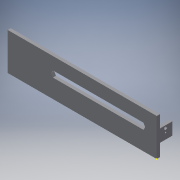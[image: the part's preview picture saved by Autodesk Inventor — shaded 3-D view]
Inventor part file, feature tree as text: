
AUTODESK INVENTOR PART (.ipt)
format: ipt  version: 2016 (Build 200138000, 138)  size: 145,920 bytes
history: native  units: in
note: dims shown in document units (in); Inventor stores cm internally (conversion verified against a paired STEP export)
features: sketch x7, extrude x5
ambient origin geometry x8: Origin, YZ Plane, XZ Plane, XY Plane, X Axis, Y Axis, Z Axis, Center Point
bodies: Solid1 (feature_tree)
feature tree (12):
  extrude  "Extrusion1"  Depth=12.0in
  sketch  "Sketch2"  dims[d2=3.0in d3=0.0in d4=7.0in]
  sketch  "Sketch3"  dims[d5=0.5in d6=0.25in d7=0.0in]
  extrude  "Extrusion2"  Depth=3.0in
  sketch  "Sketch4"  dims[d8=0.25in d9=2.0in]
  extrude  "Extrusion3"  Depth=0.25in TaperAngle=0.0deg
  extrude  "Extrusion4"  Depth=2.0in
  extrude  "Extrusion5"  Depth=1.0in TaperAngle=0.0deg
  sketch  "Sketch1"  dims[d0=0.25in d1=12.0in]
  sketch  "Sketch5"  dims[d11=1.0in d12=1.0in d13=0.0in]
  sketch  "Sketch6"  dims[d14=0.25in]
  sketch  "Sketch7"  dims[d15=0.125in d16=0.5in d17=0.2in d18=0.25in d19=0.0in d20=0.5in d21=0.5in d22=0.25in d23=0.0in d24=1.0in d25=1.22in]
